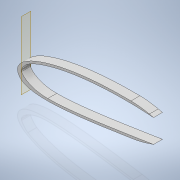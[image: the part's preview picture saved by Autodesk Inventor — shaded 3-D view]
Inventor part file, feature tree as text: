
AUTODESK INVENTOR PART (.ipt)
format: ipt  version: 2022.1 (Build 261234020, 234B)  size: 527,872 bytes
history: native  units: mm
features: sketch x6, extrude x5, thicken_offset x4, projected_geometry x2, shell x1, plane x1, other x1, fillet x1
ambient origin geometry x8: Origin, YZ Plane, XZ Plane, XY Plane, X Axis, Y Axis, Z Axis, Center Point
bodies: Solid1 (feature_tree)
feature tree (21):
  extrude  "Extrusion1"  Depth=3.0mm
  shell  "Shell1"  Thickness=1.0mm
  thicken_offset  "Thicken1"
  extrude  "Extrusion27"  TaperAngle=0.0deg  [1 undecoded]
  thicken_offset  "Thicken3"
  extrude  "Extrusion29"  Depth=30.0mm
  plane  "Work Plane5"
  other  "Bend Part2"
  thicken_offset  "Thicken5"
  extrude  "Extrusion31"  Depth=10.0mm TaperAngle=0.0deg
  thicken_offset  "Thicken6"
  extrude  "Extrusion32"  Depth=1.0mm
  fillet  "Fillet9"  Radius=1.0mm
  sketch  "Sketch3"  dims[d0=10.0mm d1=0.0mm d2=3.0mm d159=1.0mm d160=2.0mm]
  sketch  "Sketch48"  dims[d236=190.0mm d237=0.0mm d238=0.0mm]
  sketch  "Sketch55"  dims[d249=2.0mm d250=1.0mm d254=30.0mm]
  projected_geometry  "Projected Loop32"
  sketch  "Sketch57"  dims[d255=8.0mm d256=10.0mm d257=0.0mm]
  sketch  "Sketch59"  dims[d262=10.0mm d263=2.094395mm d264=1.0mm d265=1.0mm]
  sketch  "Sketch60"  dims[d272=150.0mm d273=100.0mm d274=0.0mm d282=2.5mm d283=2.5mm d284=10.0mm d285=0.0mm d286=100.0mm]
  projected_geometry  "Projected Loop35"
note: 1 required parameter value undecoded (feature->parameter linkage not recoverable at this tier; creation-order binding heuristic only, values carry confidence <= 0.55)
